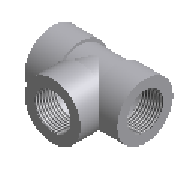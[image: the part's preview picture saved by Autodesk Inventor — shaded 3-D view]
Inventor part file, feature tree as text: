
AUTODESK INVENTOR PART (.ipt)
format: ipt  version: 2025 (Build 290162000, 162)  size: 271,872 bytes
history: native  units: mm (DEFAULTED — no unit token found)
features: other x9, revolve x4, thread x2
ambient origin geometry x8: Origin, YZ Plane, XZ Plane, XY Plane, X Axis, Y Axis, Z Axis, Center Point
bodies: Solid1 (feature_tree)
feature tree (15):
  revolve  "Revolve1"  [1 undecoded]
  revolve  "Revolve2"  [1 undecoded]
  revolve  "Revolve3"  [1 undecoded]
  revolve  "Revolve4"  [1 undecoded]
  thread  "Thread1"  [1 undecoded]
  thread  "Thread2"  [1 undecoded]
  other  "Work Axis1"
  other  "Work Point1"
  other  "Work Point2"
  other  "Work Axis2"
  other  "Work Point3"
  other  "Work Point4"
  other  "Work Axis3"
  other  "Work Point5"
  other  "Work Point6"
note: 6 required parameter values undecoded (feature->parameter linkage not recoverable at this tier; creation-order binding heuristic only, values carry confidence <= 0.55)